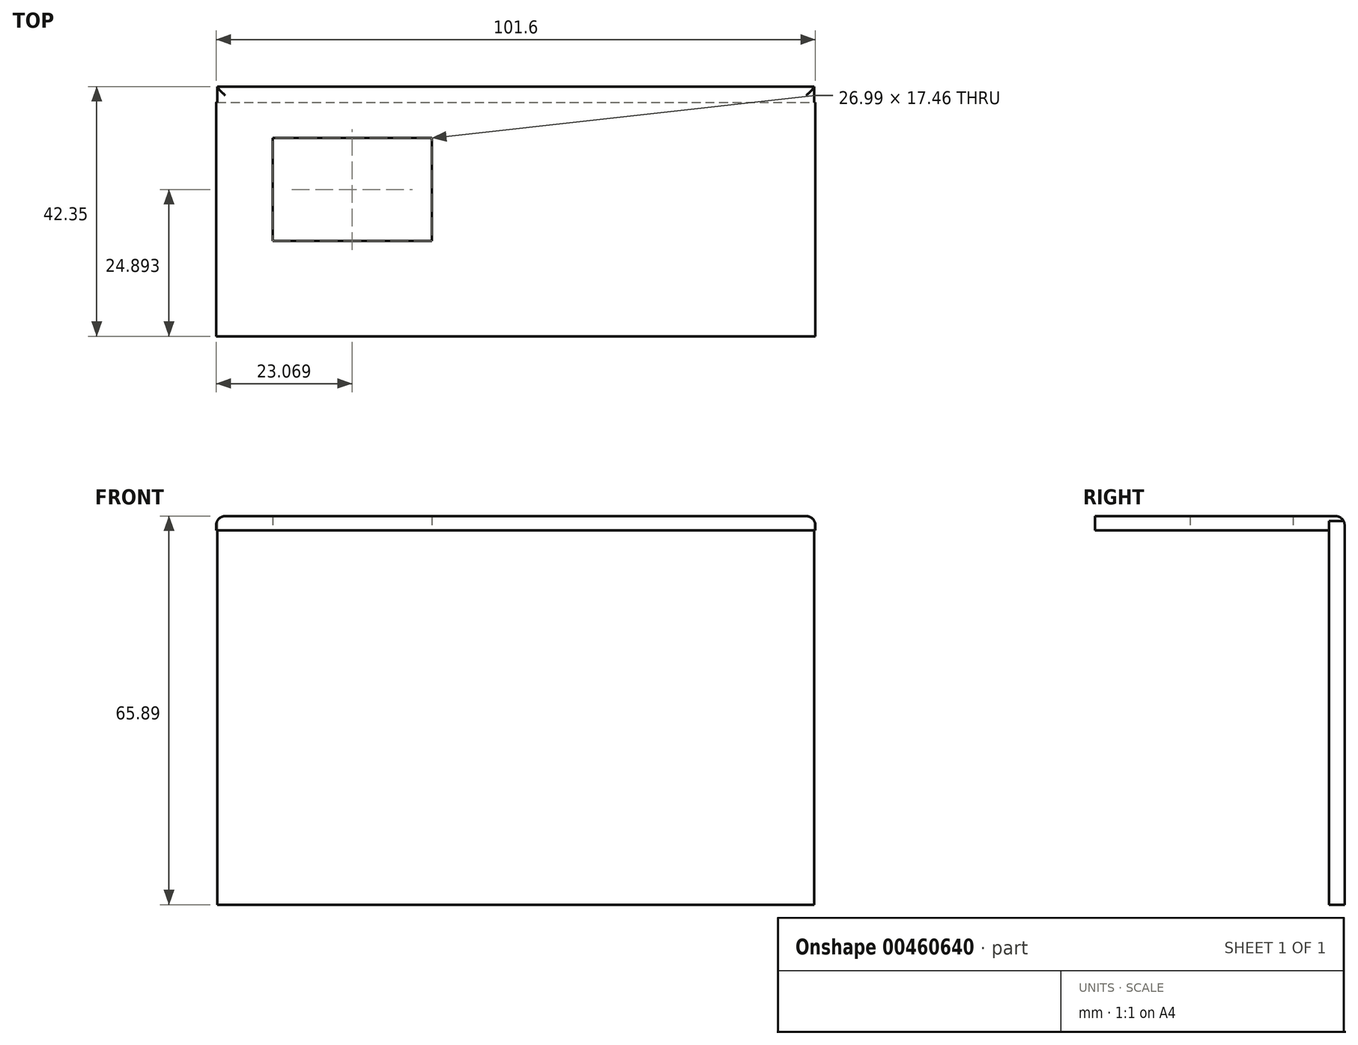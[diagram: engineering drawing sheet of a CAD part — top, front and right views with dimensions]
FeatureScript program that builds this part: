
annotation { "Feature Type Name" : "Feature", "Feature Type Description" : "" }
export const myFeature = defineFeature(function(context is Context, id is Id, definition is map)
    precondition{}
    {
        {
            var Q0;
            Q0=qCreatedBy(makeId("Top.planeOp"),FACE);
            var sketch = newSketch(context, id + "F0", { "sketchPlane" : qUnion([Q0])});
            skLineSegment(sketch, "E0.bottom", {"start": v(-50.8, 0) * mm, "end": v(50.8, 0) * mm});
            skLineSegment(sketch, "E0.top", {"start": v(-50.8, -39.67) * mm, "end": v(50.8, -39.67) * mm});
            skLineSegment(sketch, "E0.left", {"start": v(-50.8, 0) * mm, "end": v(-50.8, -39.67) * mm});
            skLineSegment(sketch, "E0.right", {"start": v(50.8, 0) * mm, "end": v(50.8, -39.67) * mm});
            skSolve(sketch);
        }
        {
            var Q0;
            Q0=qCreatedBy(makeId("Top.planeOp"),FACE);
            var sketch = newSketch(context, id + "F1", { "sketchPlane" : qUnion([Q0])});
            skLineSegment(sketch, "E1.bottom", {"start": v(-41.22, -6.05) * mm, "end": v(-14.24, -6.05) * mm});
            skLineSegment(sketch, "E1.top", {"start": v(-41.22, -23.5) * mm, "end": v(-14.24, -23.5) * mm});
            skLineSegment(sketch, "E1.left", {"start": v(-41.22, -6.05) * mm, "end": v(-41.22, -23.5) * mm});
            skLineSegment(sketch, "E1.right", {"start": v(-14.24, -6.05) * mm, "end": v(-14.24, -23.5) * mm});
            skSolve(sketch);
        }
        {
            var Q0;
            Q0 = qSketchRegion(id + "F0", true);
            extrude(context, id + "F2", {"entities" : qUnion([Q0]), "depth" : 2.38 * mm});
        }
        {
            var Q0;
            Q0 = qSketchRegion(id + "F1", true);
            extrude(context, id + "F3", {"entities" : qUnion([Q0]), "operationType" : NewBodyOperationType.REMOVE, "depth" : 27.43 * mm});
        }
        {
            var Q0;
            Q0=qCreatedBy(makeId("Top.planeOp"),FACE);
            var sketch = newSketch(context, id + "F4", { "sketchPlane" : qUnion([Q0])});
            skLineSegment(sketch, "E2.bottom", {"start": v(-50.62, 0) * mm, "end": v(50.62, 0) * mm});
            skLineSegment(sketch, "E2.top", {"start": v(-50.62, 2.68) * mm, "end": v(50.62, 2.68) * mm});
            skLineSegment(sketch, "E2.left", {"start": v(-50.62, 0) * mm, "end": v(-50.62, 2.68) * mm});
            skLineSegment(sketch, "E2.right", {"start": v(50.62, 0) * mm, "end": v(50.62, 2.68) * mm});
            skSolve(sketch);
        }
        {
            var Q0;
            Q0 = qSketchRegion(id + "F4", true);
            extrude(context, id + "F5", {"entities" : qUnion([Q0]), "operationType" : NewBodyOperationType.ADD, "depth" : 2.4 * mm, "hasSecondDirection" : true, "secondDirectionOppositeDirection" : true, "secondDirectionDepth" : 63.5 * mm});
        }
        {
            var Q0;
            Q0=makeQuery(id+"F5.opExtrude","CAP_EDGE",EDGE,{"disambiguationData":[OSD([sQuery(id+"F4.wireOp",EDGE,"E2.top")])],"isStart":false});
            var Q1;
            Q1=makeQuery(id+"F2.opExtrude","CAP_EDGE",EDGE,{"disambiguationData":[OSD([sQuery(id+"F0.wireOp",EDGE,"E0.right")])],"isStart":false});
            var Q2;
            Q2=makeQuery(id+"F2.opExtrude","CAP_EDGE",EDGE,{"disambiguationData":[OSD([sQuery(id+"F0.wireOp",EDGE,"E0.left")])],"isStart":false});
            fillet(context, id + "F6", {"entities" : qUnion([Q0, Q1, Q2]), "radius" : 1.52 * mm, "tangentPropagation" : true, "allowEdgeOverflow" : false});
        }
    });
